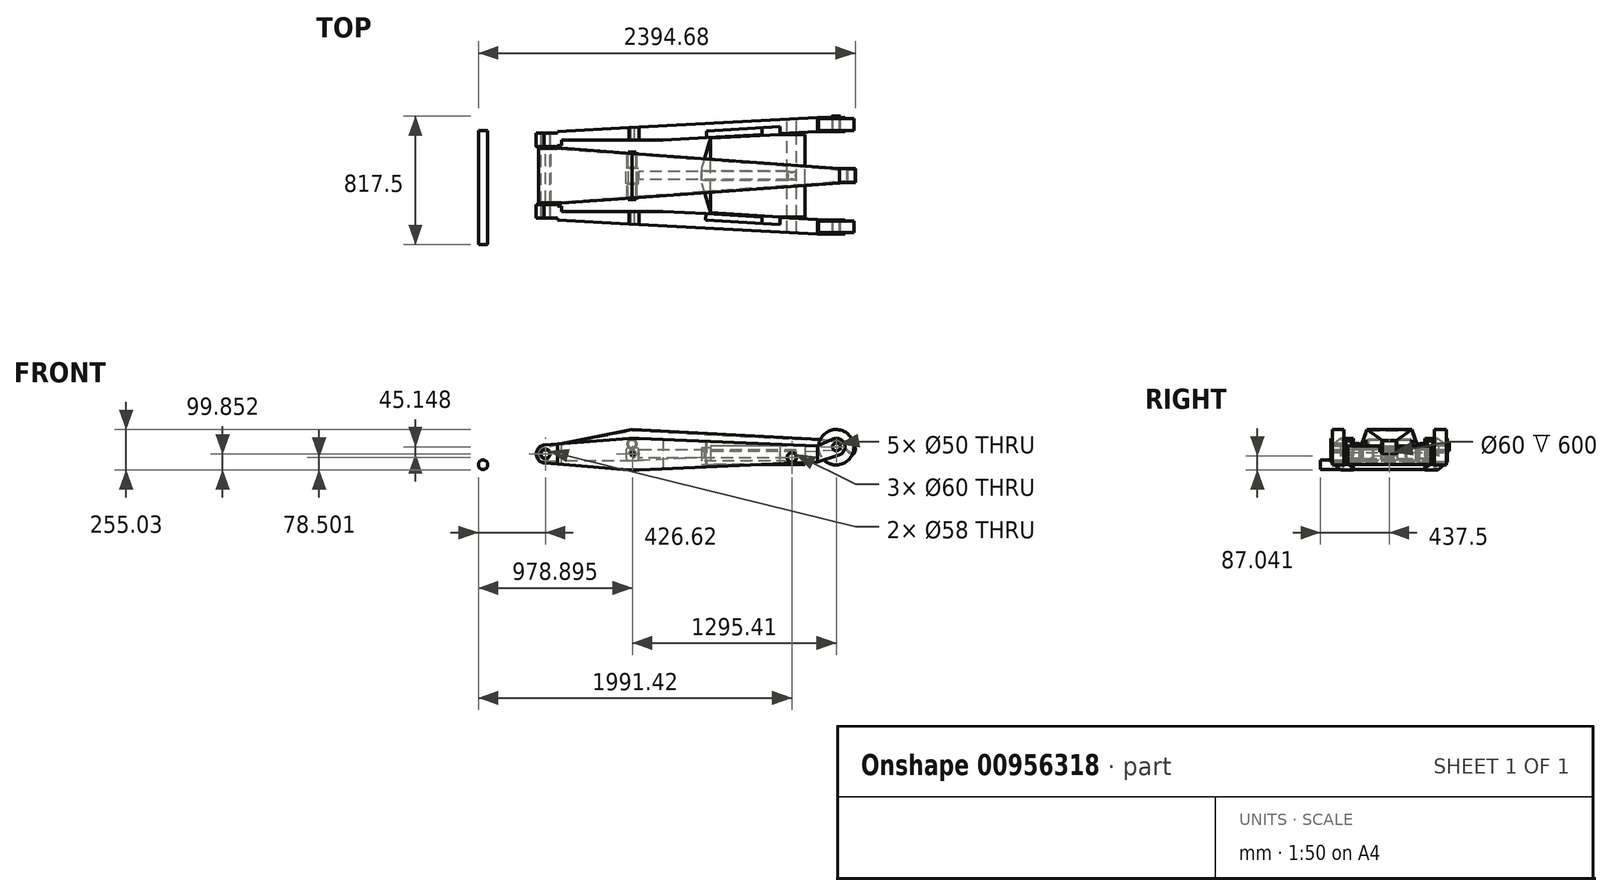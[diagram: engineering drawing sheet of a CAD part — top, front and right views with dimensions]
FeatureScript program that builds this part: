
annotation { "Feature Type Name" : "Feature", "Feature Type Description" : "" }
export const myFeature = defineFeature(function(context is Context, id is Id, definition is map)
    precondition{}
    {
        {
            var Q0;
            Q0=qCreatedBy(makeId("Top.planeOp"),FACE);
            var sketch = newSketch(context, id + "F0", { "sketchPlane" : qUnion([Q0])});
            skLineSegment(sketch, "E0", {"start": v(-223.94, 0) * mm, "end": v(2210.7, 0) * mm, "construction": true});
            skLineSegment(sketch, "E1", {"start": v(2000, 280) * mm, "end": v(1825, 280) * mm});
            skLineSegment(sketch, "E2", {"start": v(1825, 280) * mm, "end": v(2.14, 181.8) * mm});
            skLineSegment(sketch, "E3", {"start": v(2.14, 181.8) * mm, "end": v(-2.69, 271.54) * mm});
            skLineSegment(sketch, "E4", {"start": v(-2.69, 271.54) * mm, "end": v(1825, 370) * mm});
            skLineSegment(sketch, "E5", {"start": v(1825, 370) * mm, "end": v(2000, 370) * mm});
            skLineSegment(sketch, "E6", {"start": v(2000, 370) * mm, "end": v(2000, 280) * mm});
            skLineSegment(sketch, "E7.MirrorCS", {"start": v(1825, -370) * mm, "end": v(2000, -370) * mm});
            skLineSegment(sketch, "E8.MirrorCS", {"start": v(2000, -370) * mm, "end": v(2000, -280) * mm});
            skLineSegment(sketch, "E9.MirrorCS", {"start": v(1825, -280) * mm, "end": v(2.14, -181.8) * mm});
            skLineSegment(sketch, "E10.MirrorCS", {"start": v(-2.69, -271.54) * mm, "end": v(1825, -370) * mm});
            skLineSegment(sketch, "E11.MirrorCS", {"start": v(2000, -280) * mm, "end": v(1825, -280) * mm});
            skLineSegment(sketch, "E12.MirrorCS", {"start": v(2.14, -181.8) * mm, "end": v(-2.69, -271.54) * mm});
            skSolve(sketch);
        }
        {
            var Q0;
            Q0 = qSketchRegion(id + "F0", true);
            extrude(context, id + "F1", {"entities" : qUnion([Q0]), "depth" : 200 * mm, "offsetDistance" : 25 * mm});
        }
        {
            var Q0;
            Q0=qCreatedBy(makeId("Front.planeOp"),FACE);
            var sketch = newSketch(context, id + "F2", { "sketchPlane" : qUnion([Q0])});
            skLineSegment(sketch, "E13", {"start": v(0, 100) * mm, "end": v(650, 100) * mm});
            skLineSegment(sketch, "E14", {"start": v(650, 201.83) * mm, "end": v(-11.31, 150) * mm});
            skLineSegment(sketch, "E15", {"start": v(-11.31, 150) * mm, "end": v(-11.31, 247.62) * mm});
            skLineSegment(sketch, "E16", {"start": v(-11.31, 247.62) * mm, "end": v(650, 247.62) * mm});
            skLineSegment(sketch, "E17.MirrorCS", {"start": v(-11.31, -47.62) * mm, "end": v(650, -47.62) * mm});
            skLineSegment(sketch, "E18.MirrorCS", {"start": v(-11.31, 50) * mm, "end": v(-11.31, -47.62) * mm});
            skLineSegment(sketch, "E19.MirrorCS", {"start": v(650, -1.83) * mm, "end": v(-11.31, 50) * mm});
            skLineSegment(sketch, "E20", {"start": v(1823.96, 150) * mm, "end": v(650, 201.83) * mm});
            skLineSegment(sketch, "E21", {"start": v(650, 247.62) * mm, "end": v(1823.96, 247.62) * mm});
            skLineSegment(sketch, "E22.MirrorCS", {"start": v(1823.96, 50) * mm, "end": v(650, -1.83) * mm});
            skLineSegment(sketch, "E23.MirrorCS", {"start": v(1823.96, -47.62) * mm, "end": v(1823.96, -23.08) * mm});
            skLineSegment(sketch, "E24.MirrorCS", {"start": v(650, -47.62) * mm, "end": v(1823.96, -47.62) * mm});
            skPoint(sketch, "E25.start.orphan", {"position": v(1823.96, 100) * mm});
            skPoint(sketch, "E26.MirrorCS.start.orphan", {"position": v(650, 100) * mm});
            skPoint(sketch, "E27.MirrorCS.end.orphan", {"position": v(650, -1.83) * mm});
            skArc(sketch, "E28", {"start": v(1961.25, 92.45) * mm, "mid": v(1996.38, 164.63) * mm, "end": v(1922.07, 195) * mm});
            skLineSegment(sketch, "E29", {"start": v(1823.96, 150) * mm, "end": v(1922.07, 195) * mm});
            skLineSegment(sketch, "E30", {"start": v(1823.96, 50) * mm, "end": v(1961.25, 92.45) * mm});
            skLineSegment(sketch, "E31", {"start": v(1823.96, 247.62) * mm, "end": v(1945, 247.62) * mm});
            skLineSegment(sketch, "E32", {"start": v(1945, 247.62) * mm, "end": v(1945, 200) * mm});
            skLineSegment(sketch, "E33", {"start": v(1823.96, -23.08) * mm, "end": v(2024.64, -23.08) * mm});
            skLineSegment(sketch, "E34", {"start": v(2024.64, -23.08) * mm, "end": v(2024.64, 145) * mm});
            skLineSegment(sketch, "E35", {"start": v(2024.64, 145) * mm, "end": v(2000, 145) * mm});
            skLineSegment(sketch, "E36.trimOffspring", {"start": v(1976.62, 100) * mm, "end": v(2052.76, 100) * mm});
            skLineSegment(sketch, "E37", {"start": v(1945, 233.65) * mm, "end": v(2043.42, 233.65) * mm});
            skLineSegment(sketch, "E38", {"start": v(2043.42, 233.65) * mm, "end": v(2043.42, 145) * mm});
            skLineSegment(sketch, "E39", {"start": v(2043.42, 145) * mm, "end": v(2024.64, 145) * mm});
            skCircle(sketch, "E40", {"center": v(650, 100) * mm, "radius": 11 * mm});
            skCircle(sketch, "E41", {"center": v(97.31, 100) * mm, "radius": 29 * mm});
            skSolve(sketch);
        }
        {
            var Q0;
            Q0 = qSketchRegion(id + "F2", true);
            extrude(context, id + "F3", {"entities" : qUnion([Q0]), "operationType" : NewBodyOperationType.REMOVE, "endBound" : BoundingType.SYMMETRIC, "oppositeDirection" : true, "depth" : 800 * mm, "offsetDistance" : 25 * mm});
        }
        {
            var Q0;
            Q0=qCreatedBy(makeId("Front.planeOp"),FACE);
            var sketch = newSketch(context, id + "F4", { "sketchPlane" : qUnion([Q0])});
            skCircle(sketch, "E42", {"center": v(97.31, 100) * mm, "radius": 27.5 * mm});
            skSolve(sketch);
        }
        {
            var Q0;
            Q0 = qSketchRegion(id + "F4", true);
            extrude(context, id + "F5", {"entities" : qUnion([Q0]), "endBound" : BoundingType.SYMMETRIC, "depth" : 550 * mm, "offsetDistance" : 25 * mm});
        }
        {
            var Q0;
            Q0=qCreatedBy(makeId("Right.planeOp"),FACE);
            var sketch = newSketch(context, id + "F6", { "sketchPlane" : qUnion([Q0])});
            skLineSegment(sketch, "E43", {"start": v(269.68, 151.42) * mm, "end": v(269.68, 224.93) * mm});
            skLineSegment(sketch, "E44", {"start": v(269.68, 224.93) * mm, "end": v(308.83, 224.93) * mm});
            skLineSegment(sketch, "E45", {"start": v(308.83, 224.93) * mm, "end": v(308.83, -38.75) * mm});
            skLineSegment(sketch, "E46", {"start": v(308.83, -38.75) * mm, "end": v(269.68, -38.75) * mm});
            skLineSegment(sketch, "E47", {"start": v(269.68, -38.75) * mm, "end": v(269.68, 151.42) * mm});
            skLineSegment(sketch, "E48", {"start": v(0, 0) * mm, "end": v(0, 234.52) * mm});
            skLineSegment(sketch, "E49.MirrorCS", {"start": v(-269.68, -38.75) * mm, "end": v(-269.68, 151.42) * mm});
            skLineSegment(sketch, "E50.MirrorCS", {"start": v(-308.83, -38.75) * mm, "end": v(-269.68, -38.75) * mm});
            skLineSegment(sketch, "E51.MirrorCS", {"start": v(-269.68, 224.93) * mm, "end": v(-308.83, 224.93) * mm});
            skLineSegment(sketch, "E52.MirrorCS", {"start": v(-269.68, 151.42) * mm, "end": v(-269.68, 224.93) * mm});
            skLineSegment(sketch, "E53.MirrorCS", {"start": v(-308.83, 224.93) * mm, "end": v(-308.83, -38.75) * mm});
            skSolve(sketch);
        }
        {
            var Q0;
            Q0 = qSketchRegion(id + "F6", true);
            extrude(context, id + "F7", {"entities" : qUnion([Q0]), "operationType" : NewBodyOperationType.REMOVE, "depth" : 175 * mm, "offsetDistance" : 25 * mm});
        }
        {
            var Q0;
            Q0=makeQuery(id+"F7.boolean.opBoolean","COPY",FACE,{"derivedFrom":makeQuery(id+"F7.opExtrude","SWEPT_FACE",FACE,{"disambiguationData":[OSD([sQuery(id+"F6.wireOp",EDGE,"E43"),sQuery(id+"F6.wireOp",EDGE,"E47")])]})});
            var sketch = newSketch(context, id + "F8", { "sketchPlane" : qUnion([Q0])});
            skLineSegment(sketch, "E54", {"start": v(-97.31, 158.51) * mm, "end": v(-97.31, 215.85) * mm});
            skLineSegment(sketch, "E55", {"start": v(-97.31, 215.85) * mm, "end": v(-97.31, 158.51) * mm});
            skArc(sketch, "E56", {"start": v(-97.31, 158.51) * mm, "mid": v(-38.8, 100) * mm, "end": v(-97.31, 41.49) * mm});
            skLineSegment(sketch, "E57", {"start": v(-97.31, 41.49) * mm, "end": v(-97.31, 33.51) * mm});
            skLineSegment(sketch, "E58", {"start": v(-97.31, -7.13) * mm, "end": v(62.6, -7.13) * mm});
            skLineSegment(sketch, "E59", {"start": v(62.6, -7.13) * mm, "end": v(62.6, 219.33) * mm});
            skLineSegment(sketch, "E60", {"start": v(62.6, 219.33) * mm, "end": v(-97.31, 215.85) * mm});
            skLineSegment(sketch, "E61.trimOffspring", {"start": v(-97.31, 41.49) * mm, "end": v(-97.31, -32.68) * mm});
            skSolve(sketch);
        }
        {
            var Q0;
            Q0 = qSketchRegion(id + "F8", true);
            extrude(context, id + "F9", {"entities" : qUnion([Q0]), "operationType" : NewBodyOperationType.REMOVE, "endBound" : BoundingType.THROUGH_ALL, "oppositeDirection" : true, "depth" : 25 * mm, "offsetDistance" : 25 * mm, "hasSecondDirection" : true, "secondDirectionOppositeDirection" : false, "secondDirectionDepth" : 25 * mm});
        }
        {
            var Q0;
            Q0=qCreatedBy(makeId("Front.planeOp"),FACE);
            var sketch = newSketch(context, id + "F10", { "sketchPlane" : qUnion([Q0])});
            skLineSegment(sketch, "E62", {"start": v(1965.04, 186.17) * mm, "end": v(646.84, 255) * mm});
            skLineSegment(sketch, "E63", {"start": v(646.84, 255) * mm, "end": v(88.53, 144.14) * mm});
            skLineSegment(sketch, "E64", {"start": v(97.3, 55) * mm, "end": v(646.84, 55) * mm});
            skArc(sketch, "E65", {"start": v(88.53, 144.14) * mm, "mid": v(52.51, 95.6) * mm, "end": v(97.3, 55) * mm});
            skLineSegment(sketch, "E66.trimOffspring", {"start": v(646.84, 55) * mm, "end": v(2010.83, 126.48) * mm});
            skCircle(sketch, "E67", {"center": v(97.3, 100) * mm, "radius": 29.53 * mm});
            skLineSegment(sketch, "E68", {"start": v(97.3, 55) * mm, "end": v(174.3, 55) * mm});
            skLineSegment(sketch, "E69", {"start": v(2154.94, 55) * mm, "end": v(646.84, 55) * mm});
            skFitSpline(sketch, "E70", {"points": [v(1965.04, 186.17) * mm, v(2011.64, 178.92) * mm, v(2047.46, 159.58) * mm, v(2063.95, 139.3) * mm, v(2061.73, 111.08) * mm, v(2048.1, 96.5) * mm, v(2029.08, 104.74) * mm, v(2014.18, 119.64) * mm, v(2010.83, 126.48) * mm], "startDerivative": vector(279.8, -19.7) * mm, "endDerivative": vector(-34.35, 92.5) * mm});
            skCircle(sketch, "E71", {"center": v(646.84, 163.01) * mm, "radius": 25 * mm});
            skSolve(sketch);
        }
        {
            var Q0;
            Q0=makeQuery(id+"F10.imprint","IMPRINT",FACE,{"disambiguationData":[TD([[makeQuery(id+"F10.imprint","IMPRINT",EDGE,{"derivedFrom":sQuery(id+"F10.wireOp",EDGE,"E62")}),1.0]])]});
            extrude(context, id + "F11", {"entities" : qUnion([Q0]), "endBound" : BoundingType.SYMMETRIC, "depth" : 350 * mm, "offsetDistance" : 25 * mm});
        }
        {
            var Q0;
            Q0=qCreatedBy(makeId("Top.planeOp"),FACE);
            var sketch = newSketch(context, id + "F12", { "sketchPlane" : qUnion([Q0])});
            skLineSegment(sketch, "E72", {"start": v(0, 0) * mm, "end": v(2292.8, 0) * mm, "construction": true});
            skLineSegment(sketch, "E73", {"start": v(0, 0) * mm, "end": v(200, 0) * mm});
            skLineSegment(sketch, "E74", {"start": v(200, 0) * mm, "end": v(200, 174.7) * mm});
            skLineSegment(sketch, "E75", {"start": v(200, 174.7) * mm, "end": v(1968.53, 45) * mm});
            skLineSegment(sketch, "E76", {"start": v(1968.53, 45) * mm, "end": v(2101.61, 45) * mm});
            skLineSegment(sketch, "E77", {"start": v(2101.61, 45) * mm, "end": v(2101.61, 227.09) * mm});
            skLineSegment(sketch, "E78", {"start": v(2101.61, 227.09) * mm, "end": v(200, 227.09) * mm});
            skLineSegment(sketch, "E79", {"start": v(200, 227.09) * mm, "end": v(200, 174.7) * mm});
            skLineSegment(sketch, "E80.MirrorCS", {"start": v(1968.53, -45) * mm, "end": v(2101.61, -45) * mm});
            skLineSegment(sketch, "E81.MirrorCS", {"start": v(2101.61, -45) * mm, "end": v(2101.61, -227.09) * mm});
            skLineSegment(sketch, "E82.MirrorCS", {"start": v(2101.61, -227.09) * mm, "end": v(200, -227.09) * mm});
            skLineSegment(sketch, "E83.MirrorCS", {"start": v(200, -174.7) * mm, "end": v(1968.53, -45) * mm});
            skLineSegment(sketch, "E84.MirrorCS", {"start": v(200, -227.09) * mm, "end": v(200, -174.7) * mm});
            skSolve(sketch);
        }
        {
            var Q0;
            Q0 = qSketchRegion(id + "F12", true);
            extrude(context, id + "F13", {"entities" : qUnion([Q0]), "operationType" : NewBodyOperationType.REMOVE, "endBound" : BoundingType.THROUGH_ALL, "depth" : 25 * mm, "offsetDistance" : 25 * mm});
        }
        {
            var Q0;
            Q0=makeQuery(id+"F7.boolean.opBoolean","COPY",FACE,{"derivedFrom":makeQuery(id+"F7.opExtrude","SWEPT_FACE",FACE,{"disambiguationData":[OSD([sQuery(id+"F6.wireOp",EDGE,"E43"),sQuery(id+"F6.wireOp",EDGE,"E47")])]})});
            extrude(context, id + "F14", {"entities" : qUnion([Q0]), "operationType" : NewBodyOperationType.ADD, "oppositeDirection" : true, "depth" : 85 * mm, "offsetDistance" : 25 * mm});
        }
        {
            var Q0;
            Q0=makeQuery(id+"F7.boolean.opBoolean","COPY",FACE,{"derivedFrom":makeQuery(id+"F7.opExtrude","SWEPT_FACE",FACE,{"disambiguationData":[OSD([sQuery(id+"F6.wireOp",EDGE,"E49.MirrorCS"),sQuery(id+"F6.wireOp",EDGE,"E52.MirrorCS")])]})});
            extrude(context, id + "F15", {"entities" : qUnion([Q0]), "operationType" : NewBodyOperationType.ADD, "oppositeDirection" : true, "depth" : 85 * mm, "offsetDistance" : 25 * mm});
        }
        {
            var Q0;
            Q0=makeQuery(id+"F11.opExtrude","SWEPT_FACE",FACE,{"disambiguationData":[OSD([sQuery(id+"F10.wireOp",EDGE,"E66.trimOffspring")])]});
            var Q1;
            Q1=makeQuery(id+"F11.opExtrude","SWEPT_FACE",FACE,{"disambiguationData":[OSD([sQuery(id+"F10.wireOp",EDGE,"E64")])]});
            shell(context, id + "F16", {"entities" : qUnion([Q0, Q1]), "thickness" : 6.5 * mm});
        }
        {
            var Q0;
            Q0=qCreatedBy(makeId("Top.planeOp"),FACE);
            var sketch = newSketch(context, id + "F17", { "sketchPlane" : qUnion([Q0])});
            skLineSegment(sketch, "E85", {"start": v(1823.62, -278.72) * mm, "end": v(1823.62, -323.72) * mm});
            skLineSegment(sketch, "E86", {"start": v(1823.62, -323.72) * mm, "end": v(2014.36, -323.72) * mm});
            skLineSegment(sketch, "E87", {"start": v(2014.36, -323.72) * mm, "end": v(2014.36, -285.7) * mm});
            skLineSegment(sketch, "E88", {"start": v(2014.36, -285.7) * mm, "end": v(1823.62, -285.7) * mm});
            skLineSegment(sketch, "E89", {"start": v(1823.62, -285.7) * mm, "end": v(1823.62, -365.73) * mm});
            skLineSegment(sketch, "E90", {"start": v(1823.62, -365.73) * mm, "end": v(2014.36, -365.73) * mm});
            skLineSegment(sketch, "E91", {"start": v(2014.36, -365.73) * mm, "end": v(2014.36, -323.72) * mm});
            skLineSegment(sketch, "E92", {"start": v(0, 0) * mm, "end": v(2742.97, 0) * mm});
            skLineSegment(sketch, "E93.MirrorCS", {"start": v(1823.62, 278.72) * mm, "end": v(1823.62, 323.72) * mm});
            skLineSegment(sketch, "E94.MirrorCS", {"start": v(2014.36, 365.73) * mm, "end": v(2014.36, 323.72) * mm});
            skLineSegment(sketch, "E95.MirrorCS", {"start": v(2014.36, 323.72) * mm, "end": v(2014.36, 285.7) * mm});
            skLineSegment(sketch, "E96.MirrorCS", {"start": v(1823.62, 285.7) * mm, "end": v(1823.62, 365.73) * mm});
            skLineSegment(sketch, "E97.MirrorCS", {"start": v(2014.36, 285.7) * mm, "end": v(1823.62, 285.7) * mm});
            skLineSegment(sketch, "E98.MirrorCS", {"start": v(1823.62, 323.72) * mm, "end": v(2014.36, 323.72) * mm});
            skLineSegment(sketch, "E99.MirrorCS", {"start": v(1823.62, 365.73) * mm, "end": v(2014.36, 365.73) * mm});
            skSolve(sketch);
        }
        {
            var Q0;
            {var subQ5=sQuery(id+"F17.wireOp",EDGE,"E86");var subQ6=makeQuery(id+"F17.imprint","IMPRINT",EDGE,{"derivedFrom":subQ5});Q0=qUnion([makeQuery(id+"F17.imprint","IMPRINT",FACE,{"disambiguationData":[TD([[subQ6,1.0]])]}),makeQuery(id+"F17.imprint","IMPRINT",FACE,{"disambiguationData":[TD([[subQ6,-1.0]])]}),makeQuery(id+"F17.imprint","IMPRINT",FACE,{"disambiguationData":[TD([[makeQuery(id+"F17.imprint","IMPRINT",EDGE,{"derivedFrom":sQuery(id+"F17.wireOp",EDGE,"E95.MirrorCS")}),-1.0]])]}),makeQuery(id+"F17.imprint","IMPRINT",FACE,{"disambiguationData":[TD([[makeQuery(id+"F17.imprint","IMPRINT",EDGE,{"derivedFrom":sQuery(id+"F17.wireOp",EDGE,"E94.MirrorCS")}),-1.0]])]})]);}
            extrude(context, id + "F18", {"entities" : qUnion([Q0]), "operationType" : NewBodyOperationType.REMOVE, "endBound" : BoundingType.THROUGH_ALL, "depth" : 25 * mm, "offsetDistance" : 25 * mm});
        }
        {
            var Q0;
            Q0=qCreatedBy(makeId("Front.planeOp"),FACE);
            cPlane(context, id + "F19", {"entities" : qUnion([Q0]), "cplaneType" : CPlaneType.OFFSET, "offset" : 287.5 * mm, "oppositeDirection" : true, "width" : 150 * mm, "height" : 150 * mm});
        }
        {
            var Q0;
            Q0=qCreatedBy(id+"F19.planeOp",FACE);
            var sketch = newSketch(context, id + "F20", { "sketchPlane" : qUnion([Q0])});
            skCircle(sketch, "E100", {"center": v(1943.27, 142.53) * mm, "radius": 112.5 * mm});
            skCircle(sketch, "E101", {"center": v(1943.27, 142.53) * mm, "radius": 25 * mm});
            skSolve(sketch);
        }
        {
            var Q0;
            Q0 = qSketchRegion(id + "F20", true);
            extrude(context, id + "F21", {"entities" : qUnion([Q0]), "oppositeDirection" : true, "depth" : 75 * mm, "offsetDistance" : 25 * mm});
        }
        {
            var Q0;
            Q0=makeQuery(id+"F21.opExtrude","SWEPT_BODY",BODY,{"disambiguationData":[OSD([sQuery(id+"F20.wireOp",EDGE,"E100"),sQuery(id+"F20.wireOp",EDGE,"E101")])]});
            transform(context, id + "F22", {"entities" : qUnion([Q0]), "transformType" : TransformType.TRANSLATION_3D, "dx" : 0 * mm, "dy" : -650 * mm, "dz" : 0 * mm, "makeCopy" : true});
        }
        {
            var Q0;
            Q0=makeQuery(id+"F1.opExtrude","SWEPT_FACE",FACE,{"disambiguationData":[OSD([sQuery(id+"F0.wireOp",EDGE,"E5")])]});
            var sketch = newSketch(context, id + "F23", { "sketchPlane" : qUnion([Q0])});
            skCircle(sketch, "E102", {"center": v(-1945, 145) * mm, "radius": 25 * mm});
            skSolve(sketch);
        }
        {
            var Q0;
            Q0 = qSketchRegion(id + "F23", true);
            extrude(context, id + "F24", {"entities" : qUnion([Q0]), "oppositeDirection" : true, "depth" : 100 * mm, "offsetDistance" : 25 * mm, "hasSecondDirection" : true, "secondDirectionOppositeDirection" : false, "secondDirectionDepth" : 10 * mm});
        }
        {
            var Q0;
            Q0=makeQuery(id+"F1.opExtrude","SWEPT_FACE",FACE,{"disambiguationData":[OSD([sQuery(id+"F0.wireOp",EDGE,"E7.MirrorCS")])]});
            var sketch = newSketch(context, id + "F25", { "sketchPlane" : qUnion([Q0])});
            skCircle(sketch, "E103", {"center": v(1945, 145) * mm, "radius": 25 * mm});
            skSolve(sketch);
        }
        {
            var Q0;
            Q0 = qSketchRegion(id + "F25", true);
            extrude(context, id + "F26", {"entities" : qUnion([Q0]), "oppositeDirection" : true, "depth" : 100 * mm, "offsetDistance" : 25 * mm, "hasSecondDirection" : true, "secondDirectionOppositeDirection" : false, "secondDirectionDepth" : 10 * mm});
        }
        {
            var Q0;
            Q0=makeQuery(id+"F1.opExtrude","SWEPT_FACE",FACE,{"disambiguationData":[OSD([sQuery(id+"F0.wireOp",EDGE,"E5")])]});
            var sketch = newSketch(context, id + "F27", { "sketchPlane" : qUnion([Q0])});
            skCircle(sketch, "E104", {"center": v(-1945, 145) * mm, "radius": 25 * mm});
            skSolve(sketch);
        }
        {
            var Q0;
            Q0 = qSketchRegion(id + "F27", true);
            extrude(context, id + "F28", {"entities" : qUnion([Q0]), "operationType" : NewBodyOperationType.REMOVE, "endBound" : BoundingType.THROUGH_ALL, "oppositeDirection" : true, "depth" : 100 * mm, "offsetDistance" : 25 * mm});
        }
        {
            var Q0;
            Q0=qCreatedBy(makeId("Front.planeOp"),FACE);
            var sketch = newSketch(context, id + "F29", { "sketchPlane" : qUnion([Q0])});
            skCircle(sketch, "E105", {"center": v(646.83, 163.37) * mm, "radius": 25 * mm});
            skSolve(sketch);
        }
        {
            var Q0;
            Q0 = qSketchRegion(id + "F29", true);
            extrude(context, id + "F30", {"entities" : qUnion([Q0]), "endBound" : BoundingType.SYMMETRIC, "depth" : 300 * mm, "offsetDistance" : 25 * mm});
        }
        {
            var Q0;
            Q0=qCreatedBy(makeId("Front.planeOp"),FACE);
            var sketch = newSketch(context, id + "F31", { "sketchPlane" : qUnion([Q0])});
            skLineSegment(sketch, "E106.bottom", {"start": v(612.1, 129.21) * mm, "end": v(680.48, 129.21) * mm});
            skLineSegment(sketch, "E106.top", {"start": v(612.1, 199.2) * mm, "end": v(680.48, 199.2) * mm});
            skLineSegment(sketch, "E106.left", {"start": v(612.1, 129.21) * mm, "end": v(612.1, 199.2) * mm});
            skLineSegment(sketch, "E106.right", {"start": v(680.48, 129.21) * mm, "end": v(680.48, 199.2) * mm});
            skPoint(sketch, "E106.middle", {"position": v(646.29, 164.21) * mm});
            skSolve(sketch);
        }
        {
            var Q0;
            Q0 = qSketchRegion(id + "F31", true);
            extrude(context, id + "F32", {"entities" : qUnion([Q0]), "operationType" : NewBodyOperationType.REMOVE, "endBound" : BoundingType.SYMMETRIC, "oppositeDirection" : true, "depth" : 105 * mm, "offsetDistance" : 25 * mm});
        }
        {
            var Q0;
            Q0=qCreatedBy(makeId("Front.planeOp"),FACE);
            var sketch = newSketch(context, id + "F33", { "sketchPlane" : qUnion([Q0])});
            skLineSegment(sketch, "E107.bottom", {"start": v(1746.98, 149.54) * mm, "end": v(1146.98, 149.54) * mm});
            skLineSegment(sketch, "E107.top", {"start": v(1746.98, 34.54) * mm, "end": v(1146.98, 34.54) * mm});
            skLineSegment(sketch, "E107.left", {"start": v(1746.98, 149.54) * mm, "end": v(1746.98, 34.54) * mm});
            skLineSegment(sketch, "E107.right", {"start": v(1146.98, 149.54) * mm, "end": v(1146.98, 34.54) * mm});
            skSolve(sketch);
        }
        {
            var Q0;
            Q0 = qSketchRegion(id + "F33", true);
            extrude(context, id + "F34", {"entities" : qUnion([Q0]), "endBound" : BoundingType.SYMMETRIC, "depth" : 525 * mm, "offsetDistance" : 25 * mm});
        }
        {
            var Q0;
            Q0=makeQuery(id+"F34.opExtrude","SWEPT_FACE",FACE,{"disambiguationData":[OSD([sQuery(id+"F33.wireOp",EDGE,"E107.top")])]});
            var sketch = newSketch(context, id + "F35", { "sketchPlane" : qUnion([Q0])});
            skLineSegment(sketch, "E108", {"start": v(1587.72, 262.5) * mm, "end": v(1117.73, 232.37) * mm});
            skLineSegment(sketch, "E109", {"start": v(1117.73, 232.37) * mm, "end": v(1114.63, 280.78) * mm});
            skLineSegment(sketch, "E110", {"start": v(1114.63, 280.78) * mm, "end": v(1586.74, 311.04) * mm});
            skLineSegment(sketch, "E111", {"start": v(1586.74, 311.04) * mm, "end": v(1587.72, 262.5) * mm});
            skLineSegment(sketch, "E112", {"start": v(1587.72, -262.5) * mm, "end": v(1120.35, -236.3) * mm});
            skLineSegment(sketch, "E113", {"start": v(1120.35, -236.3) * mm, "end": v(1120.35, -284.74) * mm});
            skLineSegment(sketch, "E114", {"start": v(1120.35, -284.74) * mm, "end": v(1587.72, -310.92) * mm});
            skLineSegment(sketch, "E115", {"start": v(1587.72, -310.92) * mm, "end": v(1587.72, -262.5) * mm});
            skSolve(sketch);
        }
        {
            var Q0;
            Q0 = qSketchRegion(id + "F35", true);
            extrude(context, id + "F36", {"entities" : qUnion([Q0]), "operationType" : NewBodyOperationType.REMOVE, "oppositeDirection" : true, "depth" : 200 * mm, "offsetDistance" : 25 * mm});
        }
        {
            var Q0;
            Q0=makeQuery(id+"F34.opExtrude","SWEPT_FACE",FACE,{"disambiguationData":[OSD([sQuery(id+"F33.wireOp",EDGE,"E107.top")])]});
            var sketch = newSketch(context, id + "F37", { "sketchPlane" : qUnion([Q0])});
            skLineSegment(sketch, "E116", {"start": v(1146.98, -237.8) * mm, "end": v(1087.63, -48.53) * mm});
            skLineSegment(sketch, "E117", {"start": v(1087.63, 47.81) * mm, "end": v(1146.98, 234.25) * mm});
            skLineSegment(sketch, "E118", {"start": v(1146.98, 234.25) * mm, "end": v(1161.09, 235.15) * mm});
            skLineSegment(sketch, "E119", {"start": v(1161.09, 235.15) * mm, "end": v(1161.09, -237.8) * mm});
            skLineSegment(sketch, "E120", {"start": v(1161.09, -237.8) * mm, "end": v(1146.98, -237.8) * mm});
            skLineSegment(sketch, "E121", {"start": v(1087.63, -48.53) * mm, "end": v(1087.63, 47.81) * mm});
            skPoint(sketch, "E122.orphan", {"position": v(1072.4, 0) * mm});
            skSolve(sketch);
        }
        {
            var Q0;
            Q0 = qSketchRegion(id + "F37", true);
            extrude(context, id + "F38", {"entities" : qUnion([Q0]), "operationType" : NewBodyOperationType.ADD, "oppositeDirection" : true, "depth" : 105 * mm, "offsetDistance" : 25 * mm});
        }
        {
            var Q0;
            Q0=makeQuery(id+"F38.opExtrude","SWEPT_FACE",FACE,{"disambiguationData":[OSD([sQuery(id+"F37.wireOp",EDGE,"E121")])]});
            var sketch = newSketch(context, id + "F39", { "sketchPlane" : qUnion([Q0])});
            skCircle(sketch, "E123", {"center": v(0, 87.04) * mm, "radius": 30 * mm});
            skPoint(sketch, "E123.centerSnap0", {"position": v(47.81, 87.04) * mm});
            skSolve(sketch);
        }
        {
            var Q0;
            Q0 = qSketchRegion(id + "F39", true);
            extrude(context, id + "F40", {"entities" : qUnion([Q0]), "operationType" : NewBodyOperationType.REMOVE, "oppositeDirection" : true, "depth" : 600 * mm, "offsetDistance" : 25 * mm});
        }
        {
            var Q0;
            Q0=qCreatedBy(makeId("Front.planeOp"),FACE);
            var sketch = newSketch(context, id + "F41", { "sketchPlane" : qUnion([Q0])});
            skLineSegment(sketch, "E124.bottom", {"start": v(624.59, 139.85) * mm, "end": v(674.59, 139.85) * mm});
            skLineSegment(sketch, "E124.top", {"start": v(624.59, 59.85) * mm, "end": v(674.59, 59.85) * mm});
            skLineSegment(sketch, "E124.left", {"start": v(609.59, 124.85) * mm, "end": v(609.59, 74.85) * mm});
            skLineSegment(sketch, "E124.right", {"start": v(689.59, 124.85) * mm, "end": v(689.59, 74.85) * mm});
            skPoint(sketch, "E124.middle", {"position": v(649.59, 99.85) * mm});
            skCircle(sketch, "E125", {"center": v(649.59, 99.85) * mm, "radius": 25 * mm});
            skPoint(sketch, "E126.visualSharp", {"position": v(609.59, 139.85) * mm});
            skArc(sketch, "E126.filletArc", {"start": v(624.59, 139.85) * mm, "mid": v(613.98, 135.46) * mm, "end": v(609.59, 124.85) * mm});
            skPoint(sketch, "E127.visualSharp", {"position": v(609.59, 59.85) * mm});
            skArc(sketch, "E127.filletArc", {"start": v(609.59, 74.85) * mm, "mid": v(613.98, 64.25) * mm, "end": v(624.59, 59.85) * mm});
            skPoint(sketch, "E128.visualSharp", {"position": v(689.59, 139.85) * mm});
            skArc(sketch, "E128.filletArc", {"start": v(689.59, 124.85) * mm, "mid": v(685.2, 135.46) * mm, "end": v(674.59, 139.85) * mm});
            skPoint(sketch, "E129.visualSharp", {"position": v(689.59, 59.85) * mm});
            skArc(sketch, "E129.filletArc", {"start": v(674.59, 59.85) * mm, "mid": v(685.2, 64.25) * mm, "end": v(689.59, 74.85) * mm});
            skSolve(sketch);
        }
        {
            var Q0;
            Q0 = qSketchRegion(id + "F41", true);
            extrude(context, id + "F42", {"entities" : qUnion([Q0]), "endBound" : BoundingType.SYMMETRIC, "depth" : 100 * mm, "offsetDistance" : 25 * mm});
        }
        {
            var Q0;
            Q0=makeQuery(id+"F42.opExtrude","SWEPT_FACE",FACE,{"disambiguationData":[OSD([sQuery(id+"F41.wireOp",EDGE,"E124.right")])]});
            var sketch = newSketch(context, id + "F43", { "sketchPlane" : qUnion([Q0])});
            skCircle(sketch, "E130", {"center": v(0, 99.85) * mm, "radius": 25 * mm});
            skPoint(sketch, "E130.centerSnap0", {"position": v(50, 99.85) * mm});
            skPoint(sketch, "E130.centerSnap1", {"position": v(0, 74.85) * mm});
            skSolve(sketch);
        }
        {
            var Q0;
            Q0 = qSketchRegion(id + "F43", true);
            extrude(context, id + "F44", {"entities" : qUnion([Q0]), "depth" : 1000 * mm, "offsetDistance" : 25 * mm});
        }
        {
            var Q0;
            Q0=makeQuery(id+"F34.opExtrude","CAP_FACE",FACE,{"disambiguationData":[OSD([sQuery(id+"F33.wireOp",EDGE,"E107.bottom"),sQuery(id+"F33.wireOp",EDGE,"E107.top"),sQuery(id+"F33.wireOp",EDGE,"E107.left"),sQuery(id+"F33.wireOp",EDGE,"E107.right")])],"isStart":true});
            var sketch = newSketch(context, id + "F45", { "sketchPlane" : qUnion([Q0])});
            skCircle(sketch, "E131", {"center": v(-1662.11, 78.5) * mm, "radius": 30 * mm});
            skSolve(sketch);
        }
        {
            var Q0;
            Q0 = qSketchRegion(id + "F45", true);
            extrude(context, id + "F46", {"entities" : qUnion([Q0]), "operationType" : NewBodyOperationType.REMOVE, "endBound" : BoundingType.THROUGH_ALL, "oppositeDirection" : true, "depth" : 25 * mm, "offsetDistance" : 25 * mm, "hasSecondDirection" : true, "secondDirectionBound" : SecondDirectionBoundingType.THROUGH_ALL, "secondDirectionOppositeDirection" : false, "secondDirectionDepth" : 25 * mm});
        }
        {
            var Q0;
            Q0=qCreatedBy(id+"F19.planeOp",FACE);
            var sketch = newSketch(context, id + "F47", { "sketchPlane" : qUnion([Q0])});
            skCircle(sketch, "E132", {"center": v(-299.31, 31.72) * mm, "radius": 30 * mm});
            skSolve(sketch);
        }
        {
            var Q0;
            Q0 = qSketchRegion(id + "F47", true);
            extrude(context, id + "F48", {"entities" : qUnion([Q0]), "depth" : 725 * mm, "offsetDistance" : 25 * mm});
        }
    });
